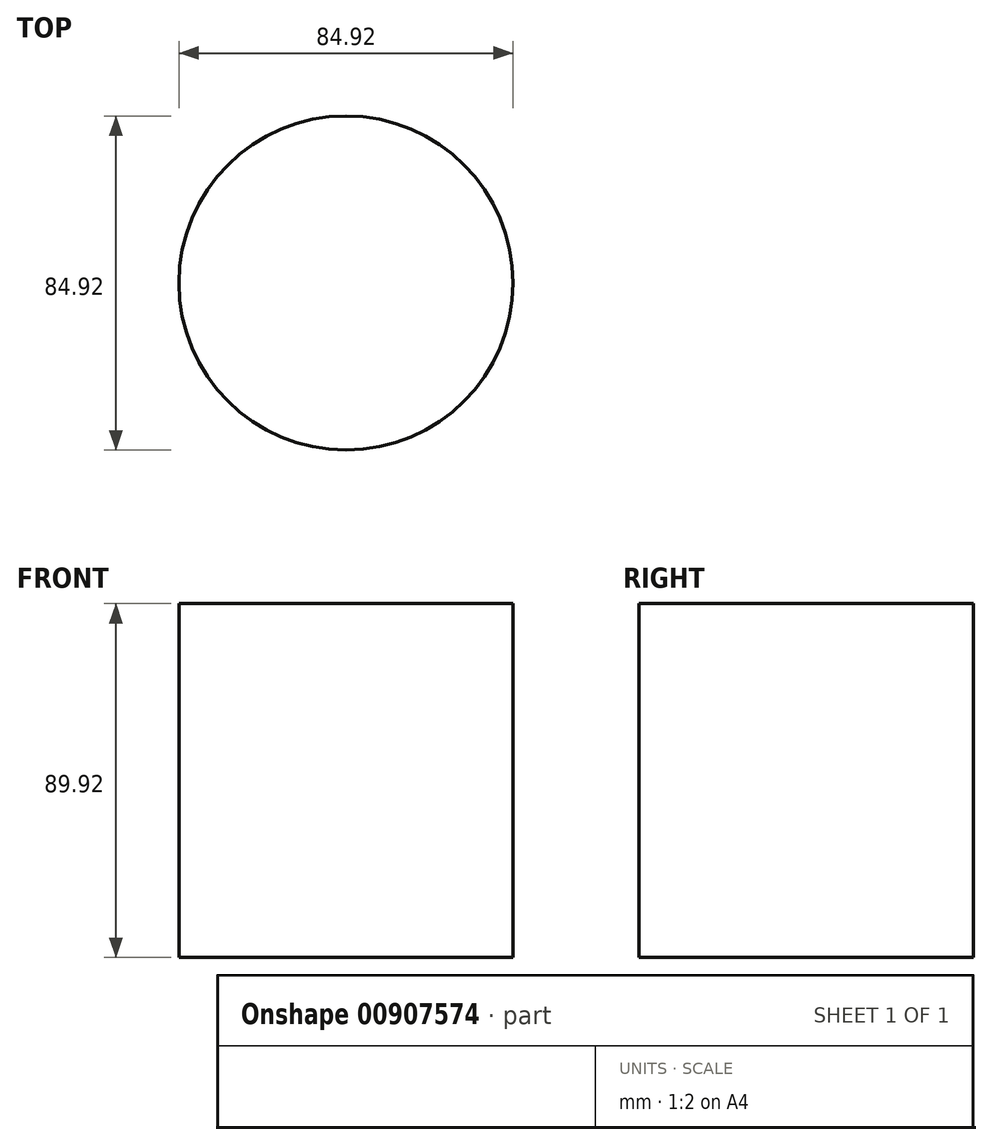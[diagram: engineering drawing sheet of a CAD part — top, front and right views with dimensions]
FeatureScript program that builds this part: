
annotation { "Feature Type Name" : "Feature", "Feature Type Description" : "" }
export const myFeature = defineFeature(function(context is Context, id is Id, definition is map)
    precondition{}
    {
        {
            var Q0;
            Q0=qCreatedBy(makeId("Top.planeOp"),FACE);
            var sketch = newSketch(context, id + "F0", { "sketchPlane" : qUnion([Q0])});
            skCircle(sketch, "E0", {"center": v(0, 0) * mm, "radius": 42.46 * mm});
            skSolve(sketch);
        }
        {
            var Q0;
            Q0 = qSketchRegion(id + "F0", true);
            extrude(context, id + "F1", {"entities" : qUnion([Q0]), "depth" : 89.92 * mm, "offsetDistance" : 25.4 * mm});
        }
    });
